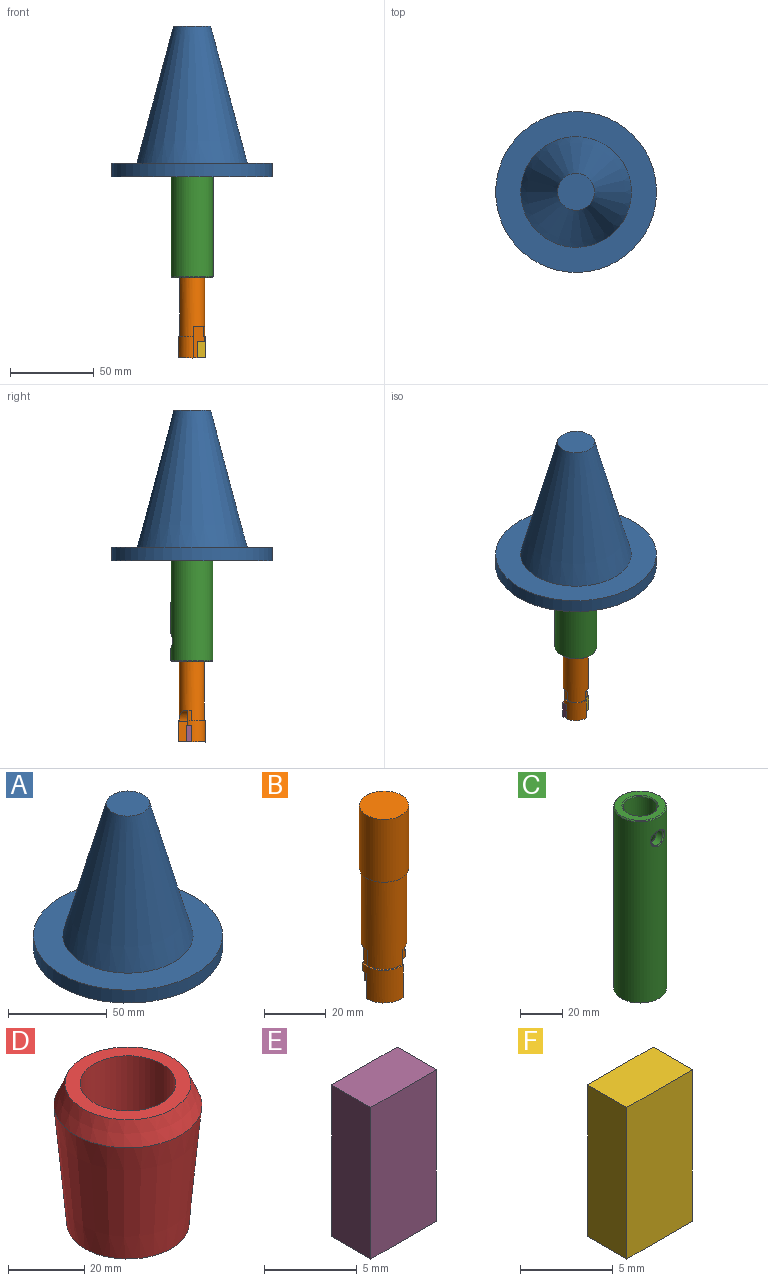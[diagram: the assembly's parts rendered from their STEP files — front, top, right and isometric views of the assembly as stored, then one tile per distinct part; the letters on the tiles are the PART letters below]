
ASSEMBLY  parts=6 mates=5
PART A: 5 faces, bbox 96x96x90 mm
  f0: plane 96x96mm, normal (0,0,-1), area 7238.2mm2, adj f1
  f1: cylinder r=48mm len=96mm, axis (0,0,-1), area 2412.7mm2, adj f0,f2
  f2: plane 96x96mm, normal (0,0,1), area 3817mm2, adj f1,f3
  f3: cone r=11.03mm half-angle=15deg, axis (0,0,-1), area 11742.2mm2, adj f2,f4
  f4: plane 22.06x22.06mm, normal (0,0,1), area 382.1mm2, adj f3
PART B: 23 faces, bbox 16x16x73 mm
  f0: plane 10.31x9mm, normal (0,0,1), area 8.5mm2, adj f2,f11,f14,f18,f22
  f1: plane 10.31x9.07mm, normal (0,0,1), area 8.6mm2, adj f3,f10,f11,f20,f21
  f2: plane 18.94x6.66mm, normal (0,1,0), area 66mm2, adj f0,f4,f8,f13,f14,f17,f20,f22
  f3: plane 19x6.66mm, normal (0,-1,0), area 76.5mm2, adj f1,f5,f6,f7,f10,f13,f18,f21
  f4: plane 5x2.3mm, normal (0,0,-1), area 11.2mm2, adj f2,f8,f9,f14
  f5: plane 5x2.3mm, normal (0,0,-1), area 11.2mm2, adj f3,f6,f10,f19
  f6: plane 10x2.3mm, normal (1,0,0), area 23mm2, adj f3,f5,f13,f19
  f7: plane 6.09x5.09mm, normal (0,0,-1), area 21.6mm2, adj f3,f11,f18
  f8: plane 10x2.3mm, normal (-1,0,0), area 23mm2, adj f2,f4,f9,f13
  f9: plane 10x5mm, normal (0,1,0), area 50mm2, adj f4,f8,f13,f14
  f10: cylinder r=8mm len=13mm, axis (0,0,1), area 183.4mm2, adj f1,f3,f5,f13,f17,f19,f20
  f11: cylinder r=7.45mm len=35mm, axis (0,0,1), area 1521.6mm2, adj f0,f1,f7,f15,f18,f20,f21,f22
  f12: plane 16x16mm, normal (0,0,1), area 201.1mm2, adj f16
  f13: plane 16x16mm, normal (0,0,-1), area 125.7mm2, adj f2,f3,f6,f8,f9,f10,f14,f17
  f14: cylinder r=8mm len=13mm, axis (0,0,1), area 183.4mm2, adj f0,f2,f4,f9,f13,f18
  f15: plane 16x16mm, normal (0,0,-1), area 26.7mm2, adj f11,f16
  f16: cylinder r=8mm len=25mm, axis (0,0,1), area 1256.6mm2, adj f12,f15
  f17: plane 12x5.64mm, normal (-1,0,0), area 67.6mm2, adj f2,f10,f13,f20
  f18: plane 19x5.64mm, normal (1,0,0), area 103.8mm2, adj f0,f3,f7,f11,f13,f14
  f19: plane 10x5mm, normal (0,-1,0), area 50mm2, adj f5,f6,f10,f13
  f20: cylinder r=7mm len=6.94mm, axis (0,-1,0), area 41.4mm2, adj f1,f2,f10,f11,f17
  f21: extruded ~6x2.3mm, area 14mm2, adj f1,f3,f11
  f22: extruded ~5.98x2.3mm, area 13.9mm2, adj f0,f2,f11
PART C: 9 faces, bbox 25x25x105 mm
  f0: cylinder r=12.5mm len=104.5mm, axis (0,0,-1), area 8139.9mm2, adj f3,f5,f8
  f1: cylinder r=8mm len=24.5mm, axis (0,0,1), area 1179.4mm2, adj f4,f6,f7
  f2: plane 24x24mm, normal (0,0,1), area 225.4mm2, adj f5,f6
  f3: plane 25x25mm, normal (0,0,-1), area 490.9mm2, adj f0
  f4: plane 16x16mm, normal (0,0,1), area 201.1mm2, adj f1
  f5: cone r=12mm half-angle=45deg, axis (0,0,-1), area 54.4mm2, adj f0,f2
  f6: cone r=8mm half-angle=45deg, axis (0,0,1), area 36.7mm2, adj f1,f2
  f7: cylinder r=4mm len=8mm, axis (0,1,0), area 100.5mm2, adj f1,f8
  f8: bspline ~9.38x9mm, area 21mm2, adj f0,f7
PART D: 5 faces, bbox 38.8x38.8x45 mm
  f0: plane 32x32mm, normal (0,0,-1), area 313.4mm2, adj f1,f3
  f1: cone r=20mm half-angle=5.1deg, axis (0,0,1), area 4243.4mm2, adj f0,f4
  f2: plane 33x33mm, normal (0,0,1), area 364.4mm2, adj f3,f4
  f3: cylinder r=12.5mm len=45mm, axis (0,0,-1), area 3534.3mm2, adj f0,f2
  f4: cone r=19.38mm half-angle=22.4deg, axis (0,0,-1), area 850.4mm2, adj f1,f2
PART E: 6 faces, bbox 5x3x10 mm
  f0: plane 10x3mm, normal (-1,0,0), area 30mm2, adj f1,f3,f4,f5
  f1: plane 5x3mm, normal (0,0,1), area 15mm2, adj f0,f2,f4,f5
  f2: plane 10x3mm, normal (1,0,0), area 30mm2, adj f1,f3,f4,f5
  f3: plane 5x3mm, normal (0,0,-1), area 15mm2, adj f0,f2,f4,f5
  f4: plane 10x5mm, normal (0,1,0), area 50mm2, adj f0,f1,f2,f3
  f5: plane 10x5mm, normal (0,-1,0), area 50mm2, adj f0,f1,f2,f3
PART F: 6 faces, bbox 5x3x10 mm
  f0: plane 10x3mm, normal (1,0,0), area 30mm2, adj f1,f3,f4,f5
  f1: plane 5x3mm, normal (0,0,1), area 15mm2, adj f0,f2,f4,f5
  f2: plane 10x3mm, normal (-1,0,0), area 30mm2, adj f1,f3,f4,f5
  f3: plane 5x3mm, normal (0,0,-1), area 15mm2, adj f0,f2,f4,f5
  f4: plane 10x5mm, normal (0,-1,0), area 50mm2, adj f0,f1,f2,f3
  f5: plane 10x5mm, normal (0,1,0), area 50mm2, adj f0,f1,f2,f3
PLACE A rot(axis=(1,0,0),0.1deg) t=(8.14,24.95,99.5)mm
PLACE B rot(axis=(1,0,0),0.1deg) t=(0.14,24.98,64.5)mm
PLACE C rot(axis=(-1,0,0),179.9deg) t=(8.14,24.9,144.5)mm fixed
PLACE D rot(axis=(-1,0,0),179.9deg) t=(8.14,24.9,144.5)mm
PLACE E rot(axis=(1,0,0),0.1deg) t=(0.14,24.98,64.5)mm
PLACE F rot(axis=(1,0,0),0.1deg) t=(0.14,24.98,64.5)mm
MATE planar D.f1 <-> C.f0  axis (0,0,1) through (8.14,24.9,144.5)mm
MATE planar E.f5 <-> B.f9  axis (0,-1,0) through (2.64,25.05,-3.5)mm
MATE planar B.f10 <-> C.f1  axis (0,0,1) through (8.14,24.98,64.5)mm
MATE planar F.f5 <-> B.f19  axis (0,1,0) through (13.64,25.05,-3.5)mm
MATE planar A.f1 <-> D.f3  axis (0,0,-1) through (8.14,24.95,99.5)mm
